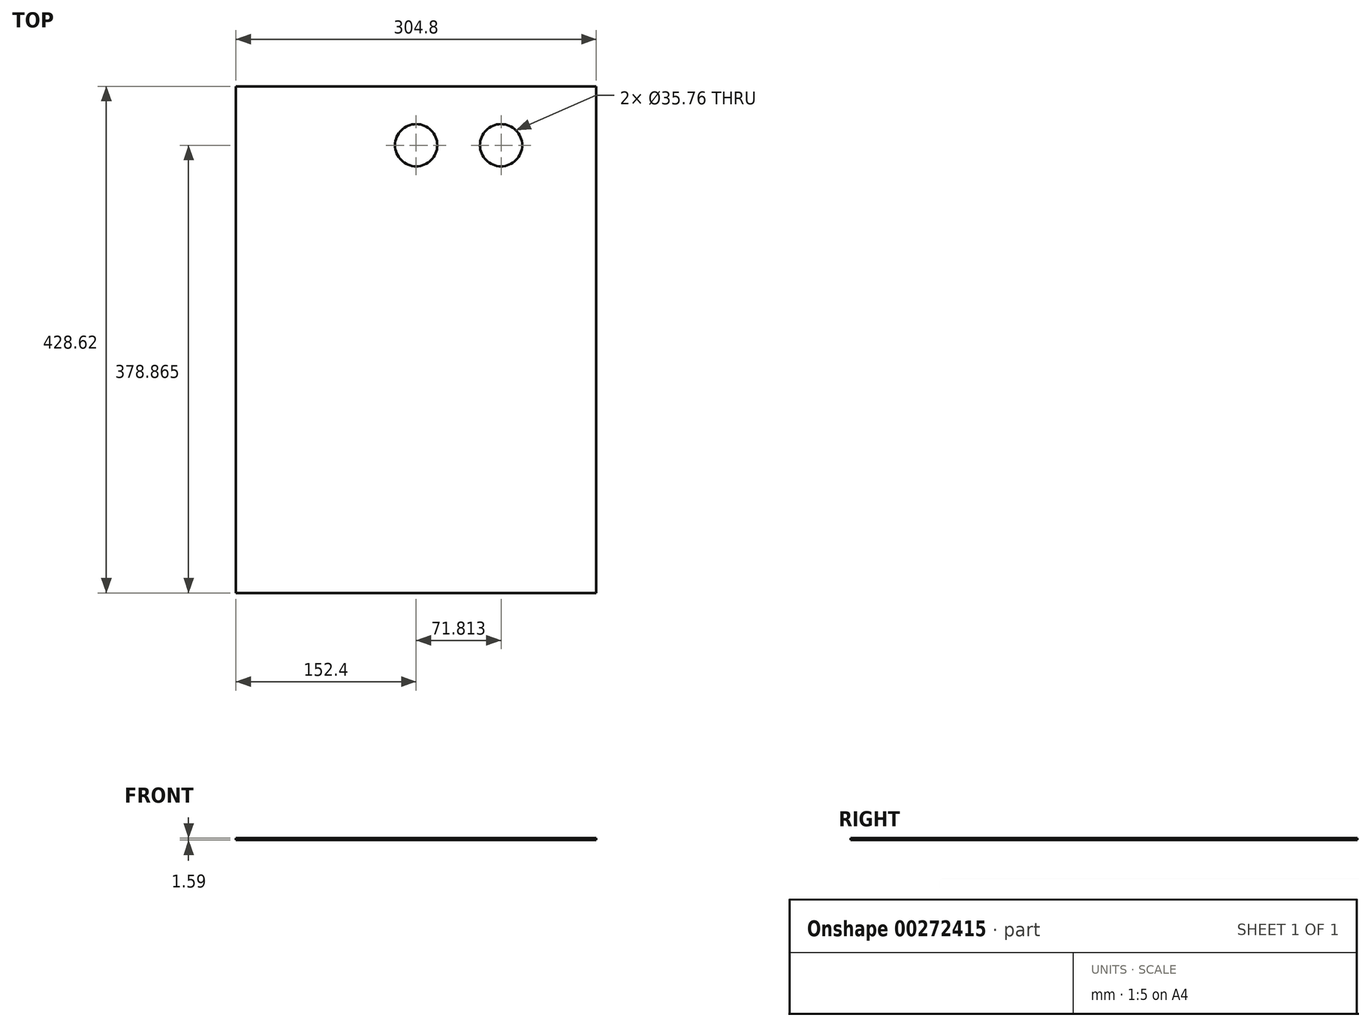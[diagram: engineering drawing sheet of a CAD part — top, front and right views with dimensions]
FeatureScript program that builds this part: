
annotation { "Feature Type Name" : "Feature", "Feature Type Description" : "" }
export const myFeature = defineFeature(function(context is Context, id is Id, definition is map)
    precondition{}
    {
        {
            var Q0;
            Q0=qCreatedBy(makeId("Top.planeOp"),FACE);
            var sketch = newSketch(context, id + "F0", { "sketchPlane" : qUnion([Q0])});
            skLineSegment(sketch, "E0.bottom", {"start": v(-152.4, 214.31) * mm, "end": v(152.4, 214.31) * mm});
            skLineSegment(sketch, "E0.top", {"start": v(-152.4, -214.31) * mm, "end": v(152.4, -214.31) * mm});
            skLineSegment(sketch, "E0.left", {"start": v(-152.4, 214.31) * mm, "end": v(-152.4, -214.31) * mm});
            skLineSegment(sketch, "E0.right", {"start": v(152.4, 214.31) * mm, "end": v(152.4, -214.31) * mm});
            skPoint(sketch, "E0.middle", {"position": v(0, 0) * mm});
            skLineSegment(sketch, "E1", {"start": v(-152.4, 114.8) * mm, "end": v(152.4, 114.8) * mm});
            skLineSegment(sketch, "E2", {"start": v(0, 114.8) * mm, "end": v(0, 214.31) * mm});
            skCircle(sketch, "E3", {"center": v(0, 164.55) * mm, "radius": 17.88 * mm});
            skLineSegment(sketch, "E4", {"start": v(71.81, 214.31) * mm, "end": v(71.81, 114.8) * mm});
            skCircle(sketch, "E5", {"center": v(71.81, 164.55) * mm, "radius": 17.88 * mm});
            skSolve(sketch);
        }
        {
            var Q0;
            Q0=makeQuery(id+"F0.imprint","IMPRINT",FACE,{"disambiguationData":[TD([[makeQuery(id+"F0.imprint","IMPRINT",EDGE,{"derivedFrom":sQuery(id+"F0.wireOp",EDGE,"E0.bottom")}),-1.0]])]});
            var Q1;
            Q1=qSketchRegion(id+"F0",true);
            extrude(context, id + "F1", {"entities" : qUnion([Q0, Q1]), "depth" : 1.59 * mm});
        }
    });
